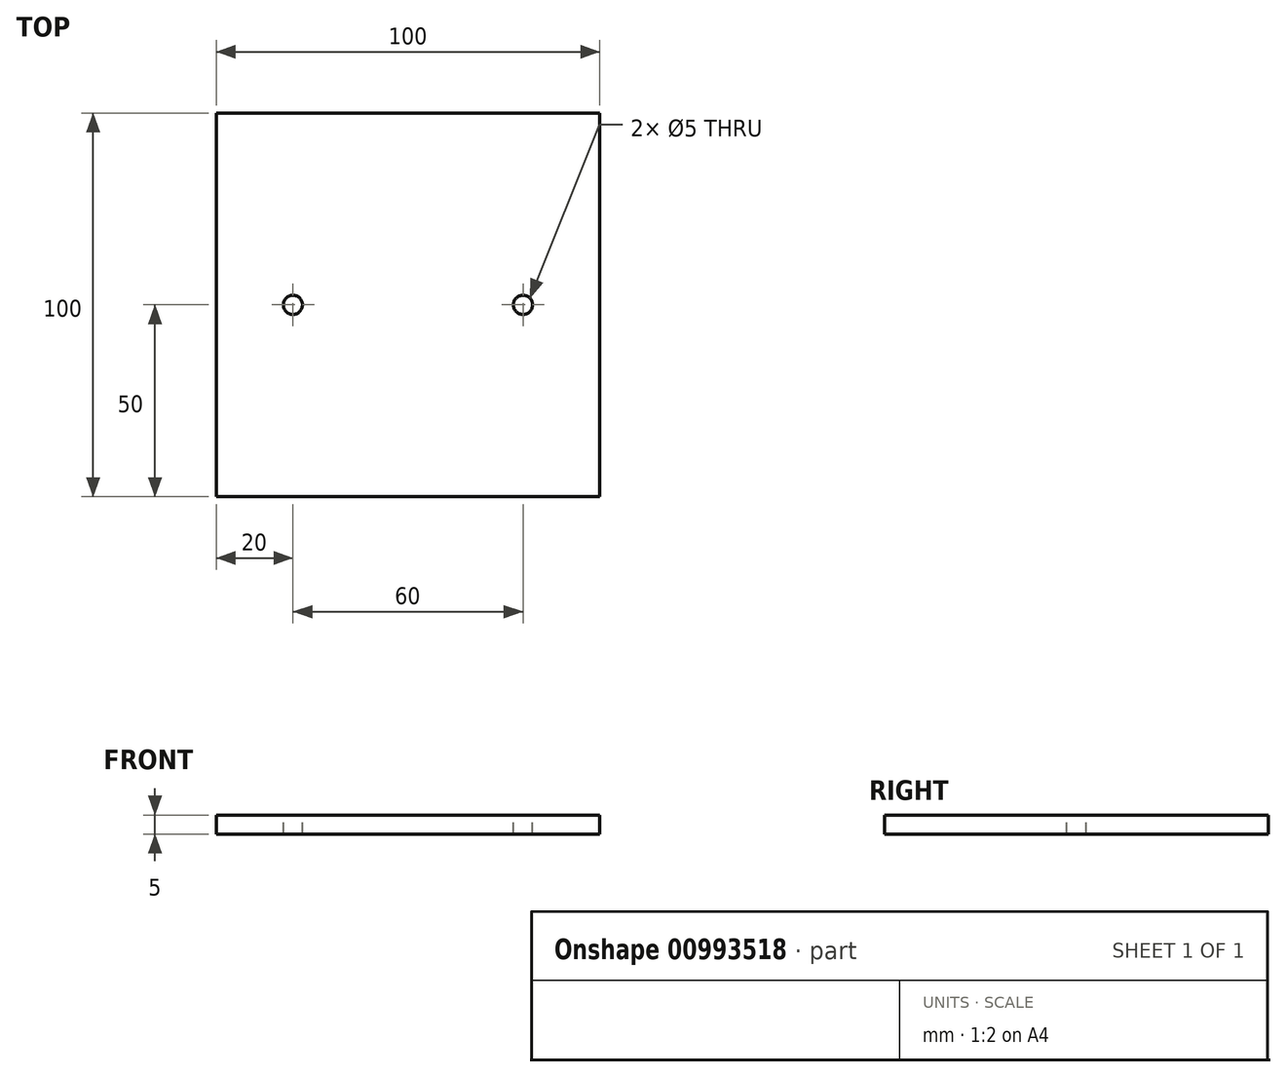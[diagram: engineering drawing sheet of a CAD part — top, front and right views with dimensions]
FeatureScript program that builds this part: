
annotation { "Feature Type Name" : "Feature", "Feature Type Description" : "" }
export const myFeature = defineFeature(function(context is Context, id is Id, definition is map)
    precondition{}
    {
        {
            var Q0;
            Q0=qCreatedBy(makeId("Top.planeOp"),FACE);
            var sketch = newSketch(context, id + "F0", { "sketchPlane" : qUnion([Q0])});
            skLineSegment(sketch, "E0.bottom", {"start": v(0, 0) * mm, "end": v(-100, 0) * mm});
            skLineSegment(sketch, "E0.top", {"start": v(0, 100) * mm, "end": v(-100, 100) * mm});
            skLineSegment(sketch, "E0.left", {"start": v(0, 0) * mm, "end": v(0, 100) * mm});
            skLineSegment(sketch, "E0.right", {"start": v(-100, 0) * mm, "end": v(-100, 100) * mm});
            skSolve(sketch);
        }
        {
            var Q0;
            Q0 = qSketchRegion(id + "F0", true);
            extrude(context, id + "F1", {"entities" : qUnion([Q0]), "depth" : 5 * mm, "offsetDistance" : 25 * mm});
        }
        {
            var Q0;
            Q0=makeQuery(id+"F1.opExtrude","CAP_FACE",FACE,{"disambiguationData":[OSD([sQuery(id+"F0.wireOp",EDGE,"E0.bottom"),sQuery(id+"F0.wireOp",EDGE,"E0.top"),sQuery(id+"F0.wireOp",EDGE,"E0.left"),sQuery(id+"F0.wireOp",EDGE,"E0.right")])],"isStart":false});
            var sketch = newSketch(context, id + "F2", { "sketchPlane" : qUnion([Q0])});
            skLineSegment(sketch, "E1", {"start": v(-100, 50) * mm, "end": v(0, 50) * mm, "construction": true});
            skCircle(sketch, "E2", {"center": v(-80, 50) * mm, "radius": 2.5 * mm});
            skCircle(sketch, "E3", {"center": v(-20, 50) * mm, "radius": 2.5 * mm});
            skSolve(sketch);
        }
        {
            var Q0;
            Q0 = qSketchRegion(id + "F2", true);
            extrude(context, id + "F3", {"entities" : qUnion([Q0]), "operationType" : NewBodyOperationType.REMOVE, "oppositeDirection" : true, "depth" : 25 * mm, "offsetDistance" : 25 * mm});
        }
    });
